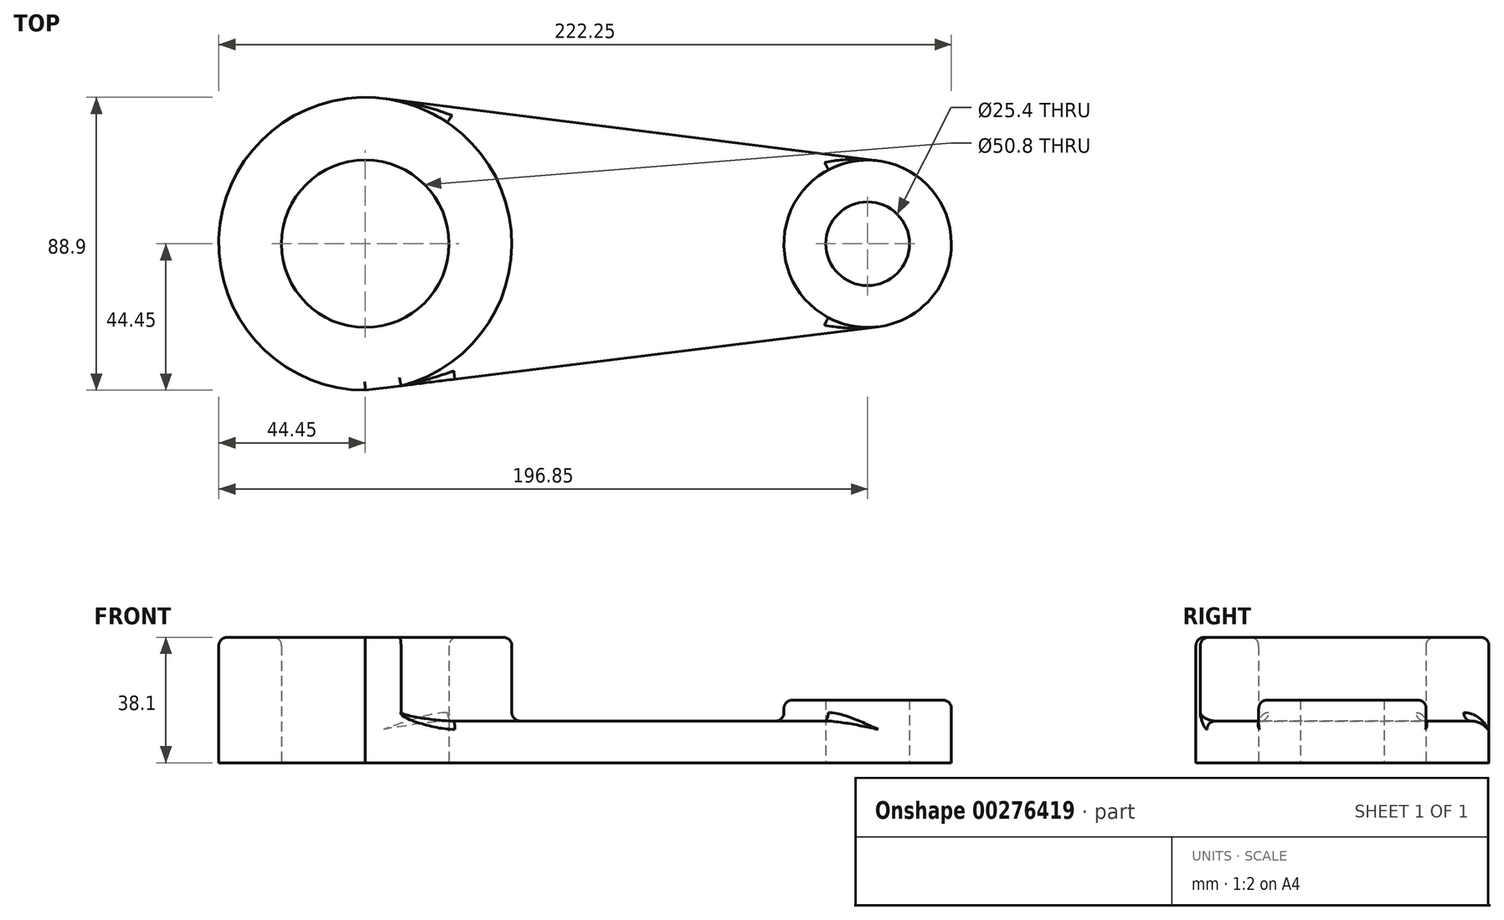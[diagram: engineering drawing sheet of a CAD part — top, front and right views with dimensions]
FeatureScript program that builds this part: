
annotation { "Feature Type Name" : "Feature", "Feature Type Description" : "" }
export const myFeature = defineFeature(function(context is Context, id is Id, definition is map)
    precondition{}
    {
        {
            var Q0;
            Q0=qCreatedBy(makeId("Top.planeOp"),FACE);
            var sketch = newSketch(context, id + "F0", { "sketchPlane" : qUnion([Q0])});
            skLineSegment(sketch, "E0", {"start": v(0, 0) * mm, "end": v(152.4, 0) * mm, "construction": true});
            skCircle(sketch, "E1", {"center": v(0, 0) * mm, "radius": 25.4 * mm});
            skCircle(sketch, "E2", {"center": v(0, 0) * mm, "radius": 44.45 * mm});
            skCircle(sketch, "E3", {"center": v(152.4, 0) * mm, "radius": 12.7 * mm});
            skCircle(sketch, "E4", {"center": v(152.4, 0) * mm, "radius": 25.4 * mm});
            skLineSegment(sketch, "E5", {"start": v(0, -44.45) * mm, "end": v(155.52, -25.2) * mm});
            skLineSegment(sketch, "E6", {"start": v(5.56, 44.1) * mm, "end": v(155.58, 25.2) * mm});
            skSolve(sketch);
        }
        {
            var Q0;
            {var subQ0=sQuery(id+"F0.wireOp",EDGE,"E6");Q0=makeQuery(id+"F0.imprint","IMPRINT",FACE,{"disambiguationData":[TD([[makeQuery(id+"F0.imprint","IMPRINT",EDGE,{"derivedFrom":subQ0}),-1.0]])]});}
            var Q1;
            Q1=makeQuery(id+"F0.imprint","IMPRINT",FACE,{"disambiguationData":[TD([[makeQuery(id+"F0.imprint","IMPRINT",EDGE,{"derivedFrom":sQuery(id+"F0.wireOp",EDGE,"E1")}),-1.0]])]});
            var Q2;
            Q2=makeQuery(id+"F0.imprint","IMPRINT",FACE,{"disambiguationData":[TD([[makeQuery(id+"F0.imprint","IMPRINT",EDGE,{"derivedFrom":sQuery(id+"F0.wireOp",EDGE,"E3")}),-1.0]])]});
            extrude(context, id + "F1", {"entities" : qUnion([Q0, Q1, Q2]), "depth" : 12.7 * mm});
        }
        {
            var Q0;
            Q0=makeQuery(id+"F1.opExtrude","CAP_FACE",FACE,{"disambiguationData":[OSD([sQuery(id+"F0.wireOp",EDGE,"E1"),sQuery(id+"F0.wireOp",EDGE,"E2"),sQuery(id+"F0.wireOp",EDGE,"E3"),sQuery(id+"F0.wireOp",EDGE,"E4"),sQuery(id+"F0.wireOp",EDGE,"E5"),sQuery(id+"F0.wireOp",EDGE,"E6")])],"isStart":false});
            var sketch = newSketch(context, id + "F2", { "sketchPlane" : qUnion([Q0])});
            skCircle(sketch, "E7.0", {"center": v(0, 0) * mm, "radius": 44.45 * mm});
            skCircle(sketch, "E8.0", {"center": v(0, 0) * mm, "radius": 25.4 * mm});
            skCircle(sketch, "E9.0", {"center": v(152.4, 0) * mm, "radius": 25.4 * mm});
            skCircle(sketch, "E10.0", {"center": v(152.4, 0) * mm, "radius": 12.7 * mm});
            skSolve(sketch);
        }
        {
            var Q0;
            Q0=makeQuery(id+"F2.imprint","IMPRINT",FACE,{"disambiguationData":[TD([[makeQuery(id+"F2.imprint","IMPRINT",EDGE,{"derivedFrom":sQuery(id+"F2.wireOp",EDGE,"E8.0")}),-1.0]])]});
            extrude(context, id + "F3", {"entities" : qUnion([Q0]), "operationType" : NewBodyOperationType.ADD, "depth" : 25.4 * mm});
        }
        {
            var Q0;
            Q0=makeQuery(id+"F2.imprint","IMPRINT",FACE,{"disambiguationData":[TD([[makeQuery(id+"F2.imprint","IMPRINT",EDGE,{"derivedFrom":sQuery(id+"F2.wireOp",EDGE,"E10.0")}),-1.0]])]});
            extrude(context, id + "F4", {"entities" : qUnion([Q0]), "operationType" : NewBodyOperationType.ADD, "depth" : 6.35 * mm});
        }
        {
            var Q0;
            Q0=makeQuery(id+"F1.opExtrude","CAP_FACE",FACE,{"disambiguationData":[OSD([sQuery(id+"F0.wireOp",EDGE,"E1"),sQuery(id+"F0.wireOp",EDGE,"E2"),sQuery(id+"F0.wireOp",EDGE,"E3"),sQuery(id+"F0.wireOp",EDGE,"E4"),sQuery(id+"F0.wireOp",EDGE,"E5"),sQuery(id+"F0.wireOp",EDGE,"E6")])],"isStart":false});
            fillet(context, id + "F5", {"entities" : qUnion([Q0]), "radius" : 2.54 * mm, "tangentPropagation" : true, "allowEdgeOverflow" : false});
        }
        {
            var Q0;
            Q0=makeQuery(id+"F3.opExtrude","CAP_FACE",FACE,{"disambiguationData":[OSD([sQuery(id+"F0.wireOp",EDGE,"E5"),sQuery(id+"F2.wireOp",EDGE,"E7.0"),sQuery(id+"F2.wireOp",EDGE,"E8.0")])],"isStart":false});
            var Q1;
            Q1=makeQuery(id+"F4.opExtrude","CAP_EDGE",EDGE,{"disambiguationData":[OSD([sQuery(id+"F2.wireOp",EDGE,"E9.0")])],"isStart":false});
            fillet(context, id + "F6", {"entities" : qUnion([Q0, Q1]), "radius" : 2.54 * mm, "tangentPropagation" : true, "allowEdgeOverflow" : false});
        }
    });
